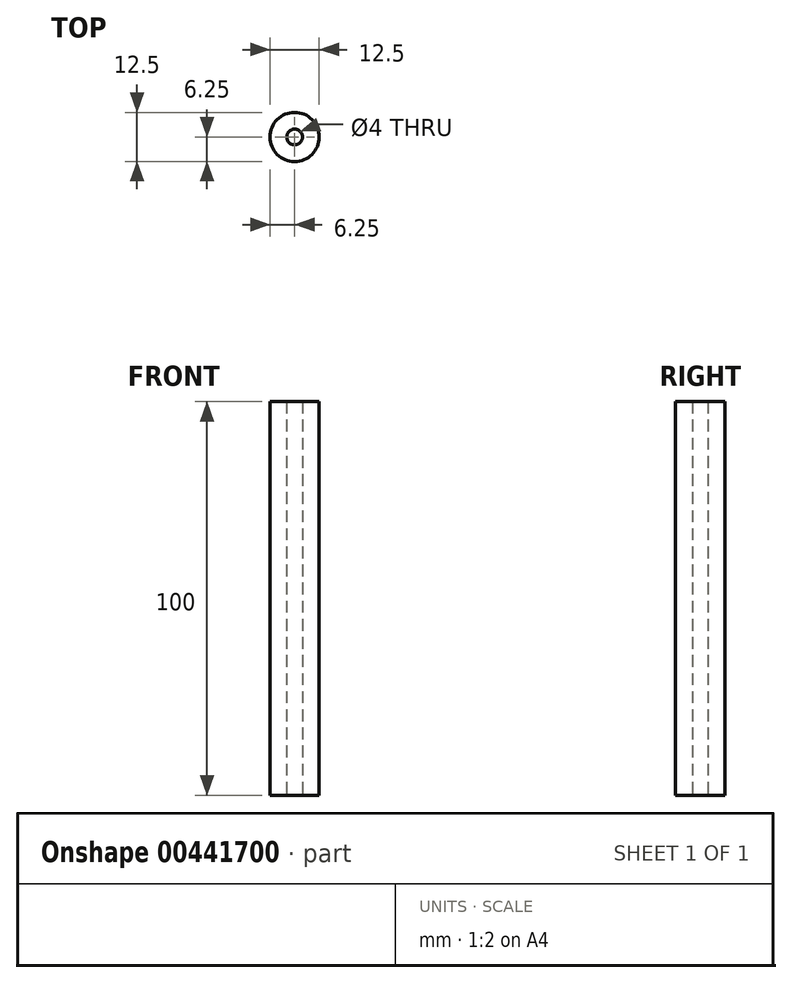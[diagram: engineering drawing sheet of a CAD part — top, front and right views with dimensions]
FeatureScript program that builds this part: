
annotation { "Feature Type Name" : "Feature", "Feature Type Description" : "" }
export const myFeature = defineFeature(function(context is Context, id is Id, definition is map)
    precondition{}
    {
        {
            var Q0;
            Q0=qCreatedBy(makeId("Top.planeOp"),FACE);
            var sketch = newSketch(context, id + "F0", { "sketchPlane" : qUnion([Q0])});
            skCircle(sketch, "E0", {"center": v(0, 0) * mm, "radius": 6.25 * mm});
            skCircle(sketch, "E1", {"center": v(0, 0) * mm, "radius": 2 * mm});
            skSolve(sketch);
        }
        {
            var Q0;
            Q0 = qSketchRegion(id + "F0", true);
            extrude(context, id + "F1", {"entities" : qUnion([Q0]), "endBound" : BoundingType.SYMMETRIC, "depth" : 100 * mm, "offsetDistance" : 25 * mm});
        }
    });
